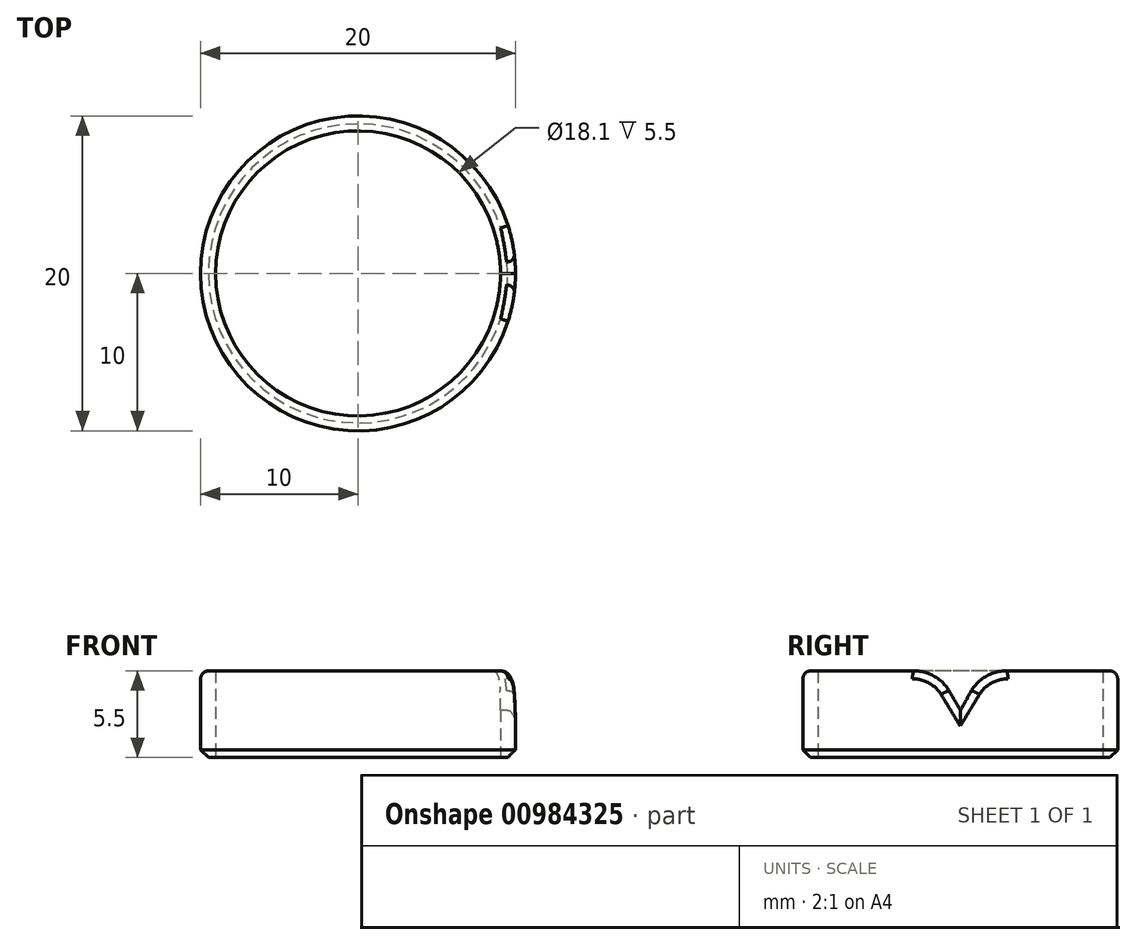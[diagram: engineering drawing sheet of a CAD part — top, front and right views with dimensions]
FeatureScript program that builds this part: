
annotation { "Feature Type Name" : "Feature", "Feature Type Description" : "" }
export const myFeature = defineFeature(function(context is Context, id is Id, definition is map)
    precondition{}
    {
        {
            var Q0;
            Q0=qCreatedBy(makeId("Top.planeOp"),FACE);
            var sketch = newSketch(context, id + "F0", { "sketchPlane" : qUnion([Q0])});
            skCircle(sketch, "E0", {"center": v(0, 0) * mm, "radius": 10 * mm});
            skCircle(sketch, "E1", {"center": v(0, 0) * mm, "radius": 9.05 * mm});
            skSolve(sketch);
        }
        {
            var Q0;
            Q0=makeQuery(id+"F0.imprint","IMPRINT",FACE,{"disambiguationData":[TD([[makeQuery(id+"F0.imprint","IMPRINT",EDGE,{"derivedFrom":sQuery(id+"F0.wireOp",EDGE,"E0")}),1.0]])]});
            extrude(context, id + "F1", {"entities" : qUnion([Q0]), "depth" : 5.5 * mm, "offsetDistance" : 25 * mm});
        }
        {
            var Q0;
            Q0=qCreatedBy(makeId("Right.planeOp"),FACE);
            var sketch = newSketch(context, id + "F2", { "sketchPlane" : qUnion([Q0])});
            skLineSegment(sketch, "E2", {"start": v(0, 3) * mm, "end": v(-1.5, 5.6) * mm});
            skLineSegment(sketch, "E3", {"start": v(-1.5, 5.6) * mm, "end": v(1.5, 5.6) * mm});
            skLineSegment(sketch, "E4", {"start": v(1.5, 5.6) * mm, "end": v(0, 3) * mm});
            skSolve(sketch);
        }
        {
            var Q0;
            Q0=makeQuery(id+"F2.imprint","IMPRINT",FACE,{"disambiguationData":[TD([[makeQuery(id+"F2.imprint","IMPRINT",EDGE,{"derivedFrom":sQuery(id+"F2.wireOp",EDGE,"E2")}),-1.0]])]});
            extrude(context, id + "F3", {"entities" : qUnion([Q0]), "operationType" : NewBodyOperationType.REMOVE, "depth" : 13.9 * mm, "offsetDistance" : 25 * mm});
        }
        {
            var Q0;
            Q0=makeQuery(id+"F3.boolean.opBoolean","INTERSECT",EDGE,{"derivedFrom":[makeQuery(id+"F1.opExtrude","CAP_FACE",FACE,{"disambiguationData":[OSD([sQuery(id+"F0.wireOp",EDGE,"E0"),sQuery(id+"F0.wireOp",EDGE,"E1")])],"isStart":false}),makeQuery(id+"F3.opExtrude","SWEPT_FACE",FACE,{"disambiguationData":[OSD([sQuery(id+"F2.wireOp",EDGE,"E2")])]})]});
            var Q1;
            Q1=makeQuery(id+"F3.boolean.opBoolean","INTERSECT",EDGE,{"derivedFrom":[makeQuery(id+"F1.opExtrude","CAP_FACE",FACE,{"disambiguationData":[OSD([sQuery(id+"F0.wireOp",EDGE,"E0"),sQuery(id+"F0.wireOp",EDGE,"E1")])],"isStart":false}),makeQuery(id+"F3.opExtrude","SWEPT_FACE",FACE,{"disambiguationData":[OSD([sQuery(id+"F2.wireOp",EDGE,"E4")])]})]});
            fillet(context, id + "F4", {"entities" : qUnion([Q0, Q1]), "radius" : 2.5 * mm, "tangentPropagation" : true, "allowEdgeOverflow" : false});
        }
        {
            var Q0;
            Q0=makeQuery(id+"F1.opExtrude","CAP_EDGE",EDGE,{"disambiguationData":[OSD([sQuery(id+"F0.wireOp",EDGE,"E0")])],"isStart":true});
            chamfer(context, id + "F5", {"entities" : qUnion([Q0]), "width" : .5 * mm, "tangentPropagation" : true});
        }
        {
            var Q0;
            Q0=makeQuery(id+"F1.opExtrude","CAP_EDGE",EDGE,{"disambiguationData":[OSD([sQuery(id+"F0.wireOp",EDGE,"E0")])],"isStart":false});
            fillet(context, id + "F6", {"entities" : qUnion([Q0]), "radius" : .5 * mm, "tangentPropagation" : true, "allowEdgeOverflow" : false});
        }
    });
